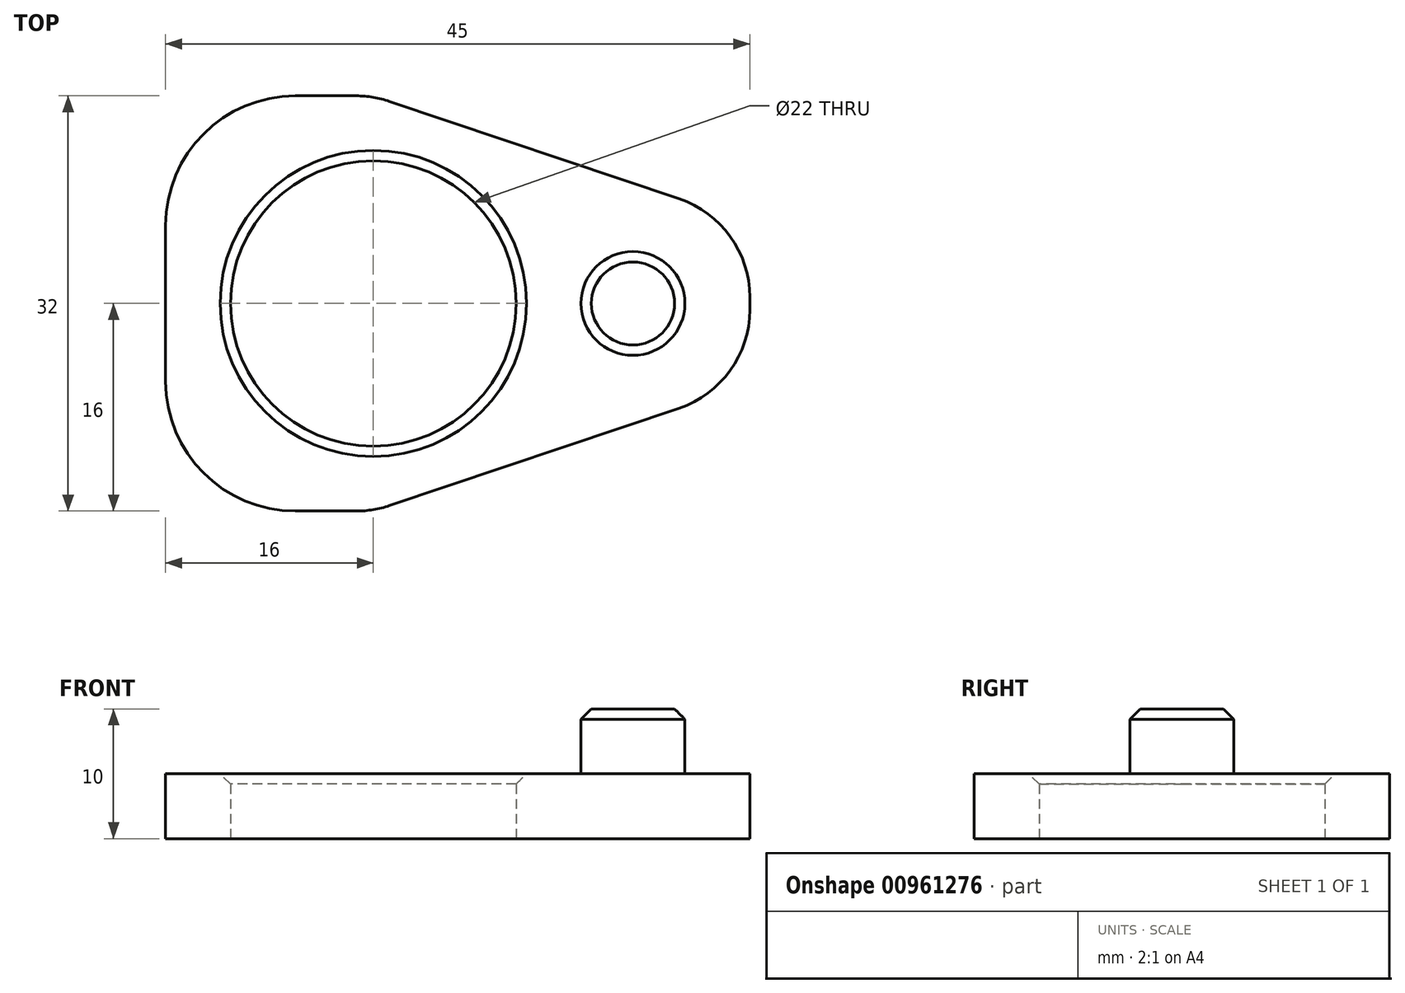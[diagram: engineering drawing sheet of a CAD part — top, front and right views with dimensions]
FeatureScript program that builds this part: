
annotation { "Feature Type Name" : "Feature", "Feature Type Description" : "" }
export const myFeature = defineFeature(function(context is Context, id is Id, definition is map)
    precondition{}
    {
        {
            var Q0;
            Q0=qCreatedBy(makeId("Top.planeOp"),FACE);
            var sketch = newSketch(context, id + "F0", { "sketchPlane" : qUnion([Q0])});
            skLineSegment(sketch, "E0.bottom", {"start": v(-6, 16) * mm, "end": v(-1.3, 16) * mm});
            skLineSegment(sketch, "E0.top", {"start": v(-6, -16) * mm, "end": v(-1.3, -16) * mm});
            skLineSegment(sketch, "E0.left", {"start": v(-16, 6) * mm, "end": v(-16, -6) * mm});
            skLineSegment(sketch, "E0.right", {"start": v(29, 0.5) * mm, "end": v(29, -0.5) * mm});
            skPoint(sketch, "E0.middle", {"position": v(0, 0) * mm});
            skCircle(sketch, "E1", {"center": v(0, 0) * mm, "radius": 11 * mm});
            skCircle(sketch, "E2", {"center": v(20, 0) * mm, "radius": 4 * mm});
            skPoint(sketch, "E3.visualSharp", {"position": v(-16, 16) * mm});
            skArc(sketch, "E3.filletArc", {"start": v(-6, 16) * mm, "mid": v(-13.07, 13.07) * mm, "end": v(-16, 6) * mm});
            skPoint(sketch, "E4.visualSharp", {"position": v(-16, -16) * mm});
            skArc(sketch, "E4.filletArc", {"start": v(-16, -6) * mm, "mid": v(-13.07, -13.07) * mm, "end": v(-6, -16) * mm});
            skLineSegment(sketch, "E5", {"start": v(23.55, 8.07) * mm, "end": v(1.24, 15.58) * mm});
            skLineSegment(sketch, "E6", {"start": v(23.55, -8.07) * mm, "end": v(1.24, -15.58) * mm});
            skLineSegment(sketch, "E7", {"start": v(29, 0) * mm, "end": v(0, 0) * mm, "construction": true});
            skPoint(sketch, "E8.visualSharp", {"position": v(29, 6.24) * mm});
            skArc(sketch, "E8.filletArc", {"start": v(29, 0.5) * mm, "mid": v(27.5, 5.16) * mm, "end": v(23.55, 8.07) * mm});
            skPoint(sketch, "E9.visualSharp", {"position": v(29, -6.24) * mm});
            skArc(sketch, "E9.filletArc", {"start": v(23.55, -8.07) * mm, "mid": v(27.5, -5.16) * mm, "end": v(29, -0.5) * mm});
            skPoint(sketch, "E10.visualSharp", {"position": v(0, -16) * mm});
            skArc(sketch, "E10.filletArc", {"start": v(-1.3, -16) * mm, "mid": v(-0.02, -15.9) * mm, "end": v(1.24, -15.58) * mm});
            skPoint(sketch, "E11.visualSharp", {"position": v(0, 16) * mm});
            skArc(sketch, "E11.filletArc", {"start": v(1.24, 15.58) * mm, "mid": v(-0.02, 15.9) * mm, "end": v(-1.3, 16) * mm});
            skLineSegment(sketch, "E12", {"start": v(0, 19.06) * mm, "end": v(0, -26.35) * mm, "construction": true});
            skSolve(sketch);
        }
        {
            var Q0;
            Q0 = qSketchRegion(id + "F0", true);
            var Q1;
            Q1=makeQuery(id+"F0.imprint","IMPRINT",FACE,{"disambiguationData":[TD([[makeQuery(id+"F0.imprint","IMPRINT",EDGE,{"derivedFrom":sQuery(id+"F0.wireOp",EDGE,"E2")}),1.0]])]});
            extrude(context, id + "F1", {"entities" : qUnion([Q0, Q1]), "depth" : 5 * mm, "offsetDistance" : 25 * mm});
        }
        {
            var Q0;
            Q0=makeQuery(id+"F0.imprint","IMPRINT",FACE,{"disambiguationData":[TD([[makeQuery(id+"F0.imprint","IMPRINT",EDGE,{"derivedFrom":sQuery(id+"F0.wireOp",EDGE,"E2")}),1.0]])]});
            var Q1;
            Q1=makeQuery(id+"F1.opExtrude","CAP_FACE",FACE,{"disambiguationData":[OSD([sQuery(id+"F0.wireOp",EDGE,"E0.bottom"),sQuery(id+"F0.wireOp",EDGE,"E0.top"),sQuery(id+"F0.wireOp",EDGE,"E0.left"),sQuery(id+"F0.wireOp",EDGE,"E0.right"),sQuery(id+"F0.wireOp",EDGE,"E1")])],"isStart":false});
            extrude(context, id + "F2", {"entities" : qUnion([Q0]), "operationType" : NewBodyOperationType.ADD, "endBound" : BoundingType.UP_TO_SURFACE, "depth" : 5 * mm, "endBoundEntityFace" : qUnion([Q1]), "hasOffset" : true, "offsetDistance" : 5 * mm, "offsetOppositeDirection" : true});
        }
        {
            var Q0;
            Q0=makeQuery(id+"F2.opExtrude","CAP_EDGE",EDGE,{"disambiguationData":[OSD([sQuery(id+"F0.wireOp",EDGE,"E2")])],"isStart":false});
            var Q1;
            Q1=makeQuery(id+"F1.opExtrude","CAP_EDGE",EDGE,{"disambiguationData":[OSD([sQuery(id+"F0.wireOp",EDGE,"E1")])],"isStart":false});
            chamfer(context, id + "F3", {"entities" : qUnion([Q0, Q1]), "width" : .8 * mm, "tangentPropagation" : true});
        }
    });
